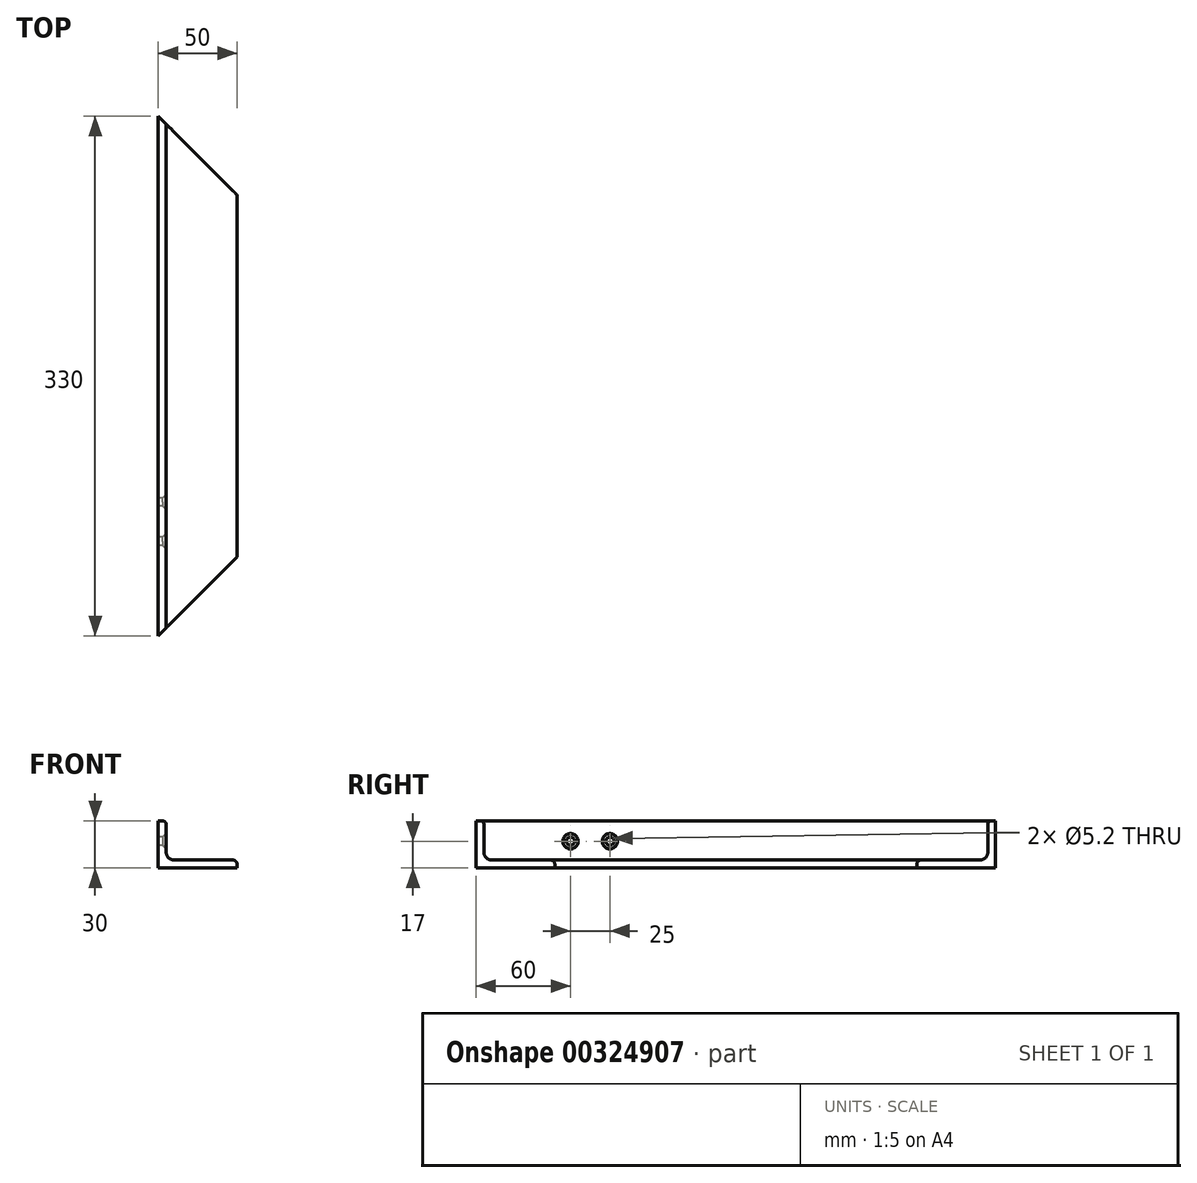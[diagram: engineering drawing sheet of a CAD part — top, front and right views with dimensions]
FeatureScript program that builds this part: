
annotation { "Feature Type Name" : "Feature", "Feature Type Description" : "" }
export const myFeature = defineFeature(function(context is Context, id is Id, definition is map)
    precondition{}
    {
        {
            var Q0;
            Q0=qCreatedBy(makeId("Front.planeOp"),FACE);
            var sketch = newSketch(context, id + "F0", { "sketchPlane" : qUnion([Q0])});
            skLineSegment(sketch, "E0.bottom", {"start": v(0, 0) * mm, "end": v(5, 0) * mm});
            skLineSegment(sketch, "E0.top", {"start": v(0, 30) * mm, "end": v(2.5, 30) * mm});
            skLineSegment(sketch, "E0.left", {"start": v(0, 0) * mm, "end": v(0, 30) * mm});
            skLineSegment(sketch, "E0.right", {"start": v(5, 10) * mm, "end": v(5, 27.5) * mm});
            skLineSegment(sketch, "E1.bottom", {"start": v(0, 0) * mm, "end": v(50, 0) * mm});
            skLineSegment(sketch, "E1.top", {"start": v(10, 5) * mm, "end": v(47.5, 5) * mm});
            skLineSegment(sketch, "E1.left", {"start": v(0, 0) * mm, "end": v(0, 5) * mm});
            skLineSegment(sketch, "E1.right", {"start": v(50, 0) * mm, "end": v(50, 2.5) * mm});
            skPoint(sketch, "E2.visualSharp", {"position": v(5, 30) * mm});
            skArc(sketch, "E2.filletArc", {"start": v(5, 27.5) * mm, "mid": v(4.27, 29.27) * mm, "end": v(2.5, 30) * mm});
            skPoint(sketch, "E3.visualSharp", {"position": v(50, 5) * mm});
            skArc(sketch, "E3.filletArc", {"start": v(50, 2.5) * mm, "mid": v(49.27, 4.27) * mm, "end": v(47.5, 5) * mm});
            skPoint(sketch, "E4.visualSharp", {"position": v(5, 5) * mm});
            skArc(sketch, "E4.filletArc", {"start": v(5, 10) * mm, "mid": v(6.46, 6.46) * mm, "end": v(10, 5) * mm});
            skSolve(sketch);
        }
        {
            var Q0;
            Q0=makeQuery(id+"F0.imprint","IMPRINT",FACE,{"disambiguationData":[TD([[makeQuery(id+"F0.imprint","IMPRINT",EDGE,{"derivedFrom":sQuery(id+"F0.wireOp",EDGE,"E0.top")}),-1.0]])]});
            extrude(context, id + "F1", {"entities" : qUnion([Q0]), "oppositeDirection" : true, "depth" : 330 * mm});
        }
        {
            var Q0;
            Q0=makeQuery(id+"F1.opExtrude","SWEPT_FACE",FACE,{"disambiguationData":[OSD([sQuery(id+"F0.wireOp",EDGE,"E0.top")])]});
            var sketch = newSketch(context, id + "F2", { "sketchPlane" : qUnion([Q0])});
            skLineSegment(sketch, "E5", {"start": v(0, 0) * mm, "end": v(72.67, 72.67) * mm});
            skLineSegment(sketch, "E6", {"start": v(0, 0) * mm, "end": v(72.67, 0) * mm});
            skLineSegment(sketch, "E7", {"start": v(72.67, 0) * mm, "end": v(72.67, 72.67) * mm});
            skLineSegment(sketch, "E8", {"start": v(-7.97, 165) * mm, "end": v(82.88, 165) * mm, "construction": true});
            skLineSegment(sketch, "E9.MirrorCS", {"start": v(72.67, 330) * mm, "end": v(72.67, 257.33) * mm});
            skLineSegment(sketch, "E10.MirrorCS", {"start": v(0, 330) * mm, "end": v(72.67, 257.33) * mm});
            skLineSegment(sketch, "E11.MirrorCS", {"start": v(0, 330) * mm, "end": v(72.67, 330) * mm});
            skSolve(sketch);
        }
        {
            var Q0;
            {var subQ0=sQuery(id+"F2.wireOp",EDGE,"E9.MirrorCS");Q0=makeQuery(id+"F2.imprint","IMPRINT",FACE,{"disambiguationData":[TD([[makeQuery(id+"F2.imprint","IMPRINT",EDGE,{"derivedFrom":subQ0}),-1.0]])]});}
            var Q1;
            {var subQ0=sQuery(id+"F2.wireOp",EDGE,"E7");Q1=makeQuery(id+"F2.imprint","IMPRINT",FACE,{"disambiguationData":[TD([[makeQuery(id+"F2.imprint","IMPRINT",EDGE,{"derivedFrom":subQ0}),1.0]])]});}
            var Q2;
            {var subQ1=sQuery(id+"F2.wireOp",EDGE,"E10.MirrorCS");var subQ2=sQuery(id+"F0.wireOp",EDGE,"E0.top");var subQ4=makeQuery(id+"F1.opExtrude","SWEPT_EDGE",EDGE,{"disambiguationData":[OSD([subQ2,sQuery(id+"F0.wireOp",EDGE,"E2.filletArc")])]});var subQ5=makeQuery(id+"F2.imprint","INTERSECT",VERTEX,{"derivedFrom":[subQ4,subQ1]});Q2=makeQuery(id+"F2.imprint","IMPRINT",FACE,{"disambiguationData":[TD([[makeQuery(id+"F2.imprint","IMPRINT",EDGE,{"disambiguationData":[TD([[subQ5,1.0]])],"derivedFrom":subQ1}),1.0]])]});}
            var Q3;
            {var subQ1=sQuery(id+"F2.wireOp",EDGE,"E5");var subQ2=sQuery(id+"F0.wireOp",EDGE,"E0.top");var subQ4=makeQuery(id+"F1.opExtrude","SWEPT_EDGE",EDGE,{"disambiguationData":[OSD([subQ2,sQuery(id+"F0.wireOp",EDGE,"E2.filletArc")])]});var subQ5=makeQuery(id+"F2.imprint","INTERSECT",VERTEX,{"derivedFrom":[subQ4,subQ1]});Q3=makeQuery(id+"F2.imprint","IMPRINT",FACE,{"disambiguationData":[TD([[makeQuery(id+"F2.imprint","IMPRINT",EDGE,{"disambiguationData":[TD([[subQ5,1.0]])],"derivedFrom":subQ1}),-1.0]])]});}
            extrude(context, id + "F3", {"entities" : qUnion([Q0, Q1, Q2, Q3]), "operationType" : NewBodyOperationType.REMOVE, "endBound" : BoundingType.THROUGH_ALL, "oppositeDirection" : true, "depth" : 25 * mm});
        }
        {
            var Q0;
            Q0=makeQuery(id+"F1.opExtrude","SWEPT_FACE",FACE,{"disambiguationData":[OSD([sQuery(id+"F0.wireOp",EDGE,"E0.left"),sQuery(id+"F0.wireOp",EDGE,"E1.left")])]});
            var sketch = newSketch(context, id + "F4", { "sketchPlane" : qUnion([Q0])});
            skLineSegment(sketch, "E12", {"start": v(134.45, 17) * mm, "end": v(-467.93, 17) * mm, "construction": true});
            skCircle(sketch, "E13", {"center": v(-60, 17) * mm, "radius": 2.6 * mm});
            skCircle(sketch, "E14", {"center": v(-85, 17) * mm, "radius": 2.6 * mm});
            skPoint(sketch, "E15", {"position": v(-72.5, 17) * mm});
            skSolve(sketch);
        }
        {
            var Q0;
            Q0=makeQuery(id+"F4.imprint","IMPRINT",FACE,{"disambiguationData":[TD([[makeQuery(id+"F4.imprint","IMPRINT",EDGE,{"derivedFrom":sQuery(id+"F4.wireOp",EDGE,"E14")}),1.0]])]});
            var Q1;
            Q1=makeQuery(id+"F4.imprint","IMPRINT",FACE,{"disambiguationData":[TD([[makeQuery(id+"F4.imprint","IMPRINT",EDGE,{"derivedFrom":sQuery(id+"F4.wireOp",EDGE,"E13")}),1.0]])]});
            extrude(context, id + "F5", {"entities" : qUnion([Q0, Q1]), "operationType" : NewBodyOperationType.REMOVE, "endBound" : BoundingType.THROUGH_ALL, "oppositeDirection" : true, "depth" : 25 * mm});
        }
        {
            var Q0;
            Q0=makeQuery(id+"F5.boolean.opBoolean","INTERSECT",EDGE,{"derivedFrom":[makeQuery(id+"F1.opExtrude","SWEPT_FACE",FACE,{"disambiguationData":[OSD([sQuery(id+"F0.wireOp",EDGE,"E0.right")])]}),makeQuery(id+"F5.opExtrude","SWEPT_FACE",FACE,{"disambiguationData":[OSD([sQuery(id+"F4.wireOp",EDGE,"E13")])]})]});
            var Q1;
            Q1=makeQuery(id+"F5.boolean.opBoolean","INTERSECT",EDGE,{"derivedFrom":[makeQuery(id+"F1.opExtrude","SWEPT_FACE",FACE,{"disambiguationData":[OSD([sQuery(id+"F0.wireOp",EDGE,"E0.right")])]}),makeQuery(id+"F5.opExtrude","SWEPT_FACE",FACE,{"disambiguationData":[OSD([sQuery(id+"F4.wireOp",EDGE,"E14")])]})]});
            chamfer(context, id + "F6", {"entities" : qUnion([Q0, Q1]), "width" : 2.25 * mm, "tangentPropagation" : true});
        }
    });
